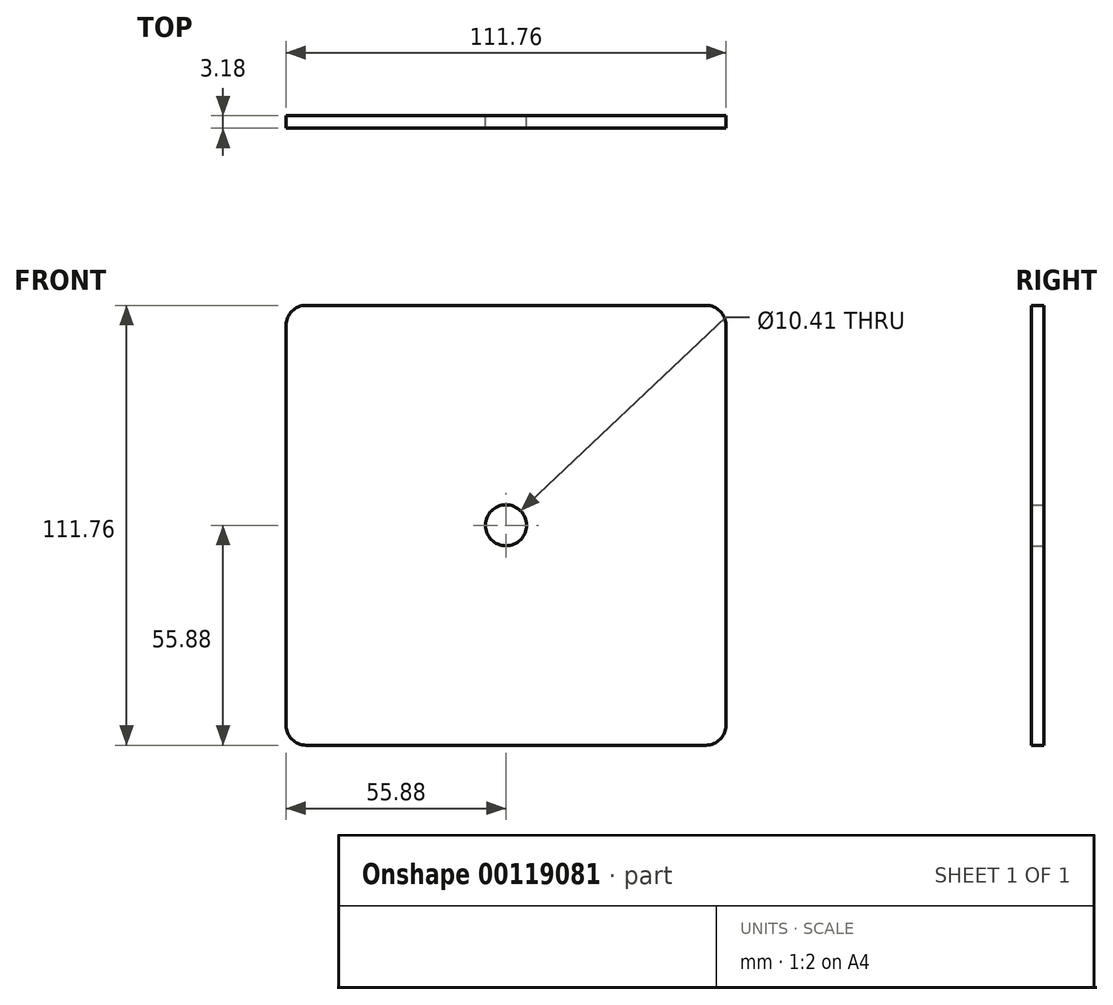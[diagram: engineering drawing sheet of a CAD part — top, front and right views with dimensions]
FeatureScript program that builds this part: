
annotation { "Feature Type Name" : "Feature", "Feature Type Description" : "" }
export const myFeature = defineFeature(function(context is Context, id is Id, definition is map)
    precondition{}
    {
        {
            var Q0;
            Q0=qCreatedBy(makeId("Front.planeOp"),FACE);
            var sketch = newSketch(context, id + "F0", { "sketchPlane" : qUnion([Q0])});
            skLineSegment(sketch, "E0.bottom", {"start": v(50.8, -55.88) * mm, "end": v(-50.8, -55.88) * mm});
            skLineSegment(sketch, "E0.top", {"start": v(50.8, 55.88) * mm, "end": v(-50.8, 55.88) * mm});
            skLineSegment(sketch, "E0.left", {"start": v(55.88, -50.8) * mm, "end": v(55.88, 50.8) * mm});
            skLineSegment(sketch, "E0.right", {"start": v(-55.88, -50.8) * mm, "end": v(-55.88, 50.8) * mm});
            skPoint(sketch, "E0.middle", {"position": v(0, 0) * mm});
            skPoint(sketch, "E1.visualSharp", {"position": v(-55.88, 55.88) * mm});
            skArc(sketch, "E1.filletArc", {"start": v(-50.8, 55.88) * mm, "mid": v(-54.4, 54.4) * mm, "end": v(-55.88, 50.8) * mm});
            skPoint(sketch, "E2.visualSharp", {"position": v(-55.88, -55.88) * mm});
            skArc(sketch, "E2.filletArc", {"start": v(-55.88, -50.8) * mm, "mid": v(-54.4, -54.4) * mm, "end": v(-50.8, -55.88) * mm});
            skPoint(sketch, "E3.visualSharp", {"position": v(55.88, -55.88) * mm});
            skArc(sketch, "E3.filletArc", {"start": v(50.8, -55.88) * mm, "mid": v(54.4, -54.4) * mm, "end": v(55.88, -50.8) * mm});
            skPoint(sketch, "E4.visualSharp", {"position": v(55.88, 55.88) * mm});
            skArc(sketch, "E4.filletArc", {"start": v(55.88, 50.8) * mm, "mid": v(54.4, 54.4) * mm, "end": v(50.8, 55.88) * mm});
            skCircle(sketch, "E5", {"center": v(0, 0) * mm, "radius": 5.2 * mm});
            skSolve(sketch);
        }
        {
            var Q0;
            Q0=makeQuery(id+"F0.imprint","IMPRINT",FACE,{"disambiguationData":[TD([[makeQuery(id+"F0.imprint","IMPRINT",EDGE,{"derivedFrom":sQuery(id+"F0.wireOp",EDGE,"E0.bottom")}),-1.0]])]});
            extrude(context, id + "F1", {"entities" : qUnion([Q0]), "depth" : 3.17 * mm});
        }
    });
